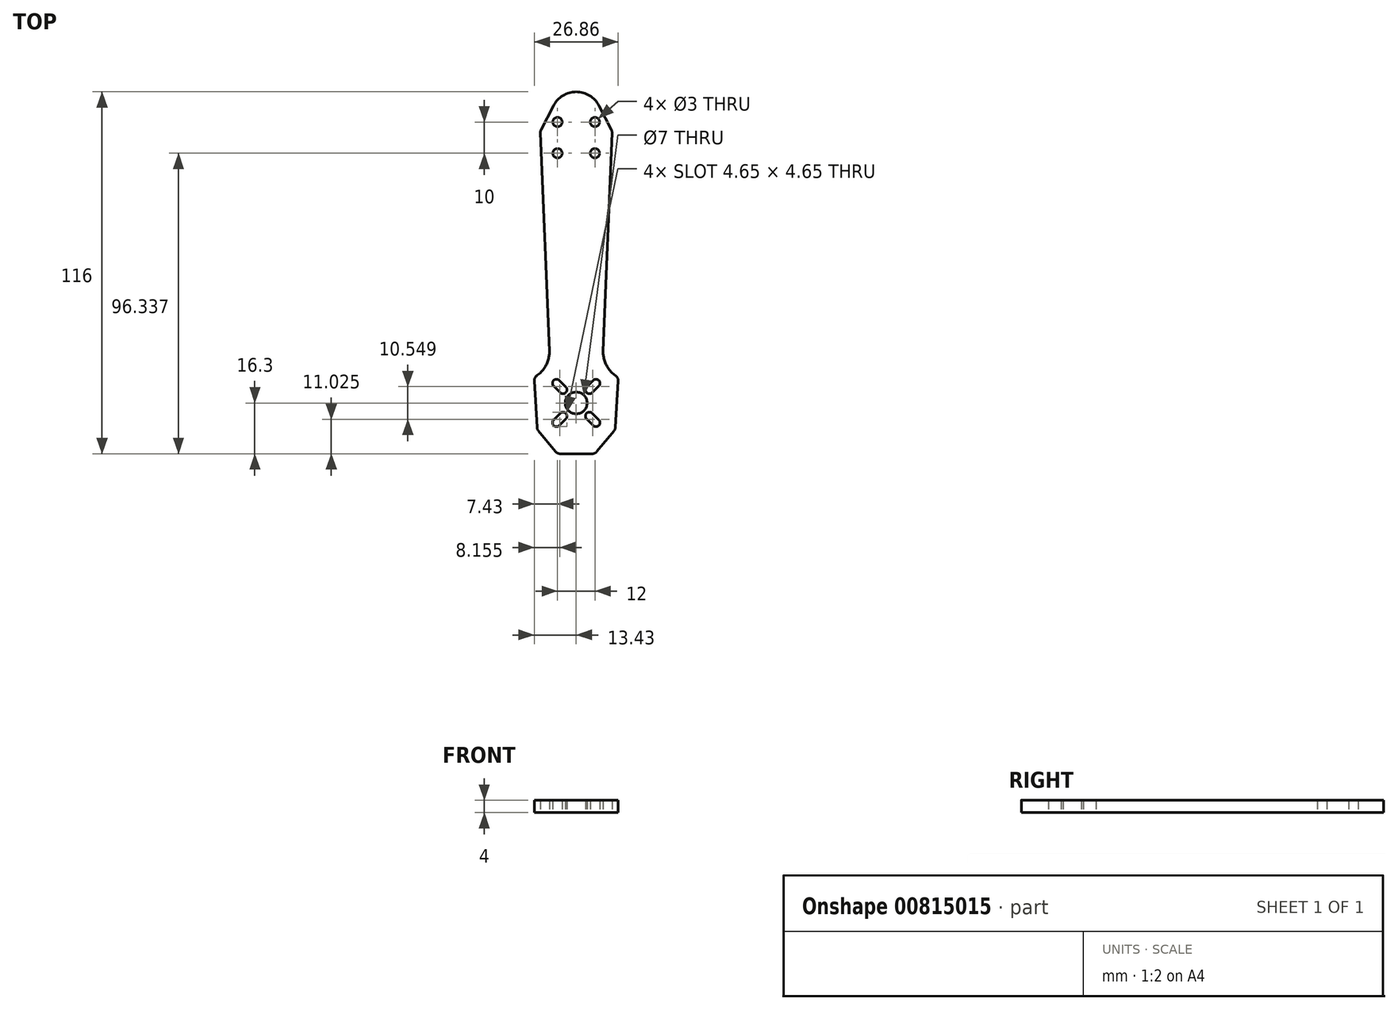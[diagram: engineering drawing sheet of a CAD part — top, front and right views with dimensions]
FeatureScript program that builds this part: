
annotation { "Feature Type Name" : "Feature", "Feature Type Description" : "" }
export const myFeature = defineFeature(function(context is Context, id is Id, definition is map)
    precondition{}
    {
        {
            var Q0;
            Q0=qCreatedBy(makeId("Top.planeOp"),FACE);
            var sketch = newSketch(context, id + "F0", { "sketchPlane" : qUnion([Q0])});
            skLineSegment(sketch, "E0", {"start": v(0, -16.3) * mm, "end": v(0, 99.7) * mm, "construction": true});
            skCircle(sketch, "E1", {"center": v(0, 0) * mm, "radius": 3.5 * mm});
            skLineSegment(sketch, "E2", {"start": v(-4.49, -4.49) * mm, "end": v(4.49, 4.49) * mm, "construction": true});
            skLineSegment(sketch, "E3", {"start": v(-4.02, 4.02) * mm, "end": v(4.02, -4.02) * mm, "construction": true});
            skLineSegment(sketch, "E4", {"start": v(4.25, -4.25) * mm, "end": v(6.3, -6.3) * mm, "construction": true});
            skArc(sketch, "E5.0.startCap", {"start": v(3.33, -5.17) * mm, "mid": v(3.33, -3.33) * mm, "end": v(5.17, -3.33) * mm});
            skArc(sketch, "E5.0.endCap", {"start": v(7.22, -5.38) * mm, "mid": v(7.22, -7.22) * mm, "end": v(5.38, -7.22) * mm});
            skLineSegment(sketch, "E5.0.left", {"start": v(5.17, -3.33) * mm, "end": v(7.22, -5.38) * mm});
            skLineSegment(sketch, "E5.0.right", {"start": v(3.33, -5.17) * mm, "end": v(5.38, -7.22) * mm});
            skLineSegment(sketch, "E6", {"start": v(-4.25, -4.25) * mm, "end": v(-6.3, -6.3) * mm, "construction": true});
            skArc(sketch, "E7.0.startCap", {"start": v(-5.17, -3.33) * mm, "mid": v(-3.33, -3.33) * mm, "end": v(-3.33, -5.17) * mm});
            skArc(sketch, "E7.0.endCap", {"start": v(-5.38, -7.22) * mm, "mid": v(-7.22, -7.22) * mm, "end": v(-7.22, -5.38) * mm});
            skLineSegment(sketch, "E7.0.left", {"start": v(-3.33, -5.17) * mm, "end": v(-5.38, -7.22) * mm});
            skLineSegment(sketch, "E7.0.right", {"start": v(-5.17, -3.33) * mm, "end": v(-7.22, -5.38) * mm});
            skLineSegment(sketch, "E8.MirrorCS", {"start": v(-4.25, 4.25) * mm, "end": v(-6.3, 6.3) * mm, "construction": true});
            skArc(sketch, "E9.MirrorCS", {"start": v(-5.17, 3.33) * mm, "mid": v(-3.33, 3.33) * mm, "end": v(-3.33, 5.17) * mm});
            skArc(sketch, "E10.MirrorCS", {"start": v(-5.38, 7.22) * mm, "mid": v(-7.22, 7.22) * mm, "end": v(-7.22, 5.38) * mm});
            skLineSegment(sketch, "E11.MirrorCS", {"start": v(-3.33, 5.17) * mm, "end": v(-5.38, 7.22) * mm});
            skLineSegment(sketch, "E12.MirrorCS", {"start": v(-5.17, 3.33) * mm, "end": v(-7.22, 5.38) * mm});
            skLineSegment(sketch, "E13.MirrorCS", {"start": v(5.17, 3.33) * mm, "end": v(7.22, 5.38) * mm});
            skLineSegment(sketch, "E14.MirrorCS", {"start": v(4.25, 4.25) * mm, "end": v(6.3, 6.3) * mm, "construction": true});
            skArc(sketch, "E15.MirrorCS", {"start": v(7.22, 5.38) * mm, "mid": v(7.22, 7.22) * mm, "end": v(5.38, 7.22) * mm});
            skArc(sketch, "E16.MirrorCS", {"start": v(3.33, 5.17) * mm, "mid": v(3.33, 3.33) * mm, "end": v(5.17, 3.33) * mm});
            skLineSegment(sketch, "E17.MirrorCS", {"start": v(3.33, 5.17) * mm, "end": v(5.38, 7.22) * mm});
            skCircle(sketch, "E18.1", {"center": v(6, 80.04) * mm, "radius": 1.5 * mm});
            skCircle(sketch, "E18.2", {"center": v(-6, 80.04) * mm, "radius": 1.5 * mm});
            skCircle(sketch, "E18.3", {"center": v(6, 90.04) * mm, "radius": 1.5 * mm});
            skCircle(sketch, "E18.4", {"center": v(-6, 90.04) * mm, "radius": 1.5 * mm});
            skLineSegment(sketch, "E19.bottom", {"start": v(6, 80.04) * mm, "end": v(-6, 80.04) * mm, "construction": true});
            skLineSegment(sketch, "E19.top", {"start": v(6, 90.04) * mm, "end": v(-6, 90.04) * mm, "construction": true});
            skLineSegment(sketch, "E19.left", {"start": v(6, 80.04) * mm, "end": v(6, 90.04) * mm, "construction": true});
            skLineSegment(sketch, "E19.right", {"start": v(-6, 80.04) * mm, "end": v(-6, 90.04) * mm, "construction": true});
            skPoint(sketch, "E19.middle", {"position": v(0, 85.04) * mm});
            skLineSegment(sketch, "E20", {"start": v(-6, -16.3) * mm, "end": v(-12.5, -8.5) * mm});
            skLineSegment(sketch, "E21", {"start": v(-12.5, -8.5) * mm, "end": v(-13.5, 8.2) * mm});
            skLineSegment(sketch, "E22", {"start": v(-8.6, 16.7) * mm, "end": v(-11.5, 87.04) * mm});
            skLineSegment(sketch, "E23", {"start": v(-11.5, 87.04) * mm, "end": v(-7.3, 95.24) * mm});
            skFitSpline(sketch, "E24", {"points": [v(-8.6, 16.7) * mm, v(-13.5, 8.2) * mm], "startDerivative": vector(0.32, -7.88) * mm, "endDerivative": vector(-11.17, -5.98) * mm});
            skLineSegment(sketch, "E25.MirrorCS", {"start": v(6, -16.3) * mm, "end": v(12.5, -8.5) * mm});
            skLineSegment(sketch, "E26.MirrorCS", {"start": v(12.5, -8.5) * mm, "end": v(13.5, 8.2) * mm});
            skFitSpline(sketch, "E27.MirrorCS", {"points": [v(8.6, 16.7) * mm, v(13.5, 8.2) * mm], "startDerivative": vector(-0.32, -7.88) * mm, "endDerivative": vector(11.17, -5.98) * mm});
            skLineSegment(sketch, "E28.MirrorCS", {"start": v(8.6, 16.7) * mm, "end": v(11.5, 87.04) * mm});
            skLineSegment(sketch, "E29.MirrorCS", {"start": v(11.5, 87.04) * mm, "end": v(7.3, 95.24) * mm});
            skArc(sketch, "E30", {"start": v(7.3, 95.24) * mm, "mid": v(0, 99.7) * mm, "end": v(-7.3, 95.24) * mm});
            skLineSegment(sketch, "E31", {"start": v(0, -16.3) * mm, "end": v(6, -16.3) * mm});
            skLineSegment(sketch, "E32.MirrorCS", {"start": v(0, -16.3) * mm, "end": v(-6, -16.3) * mm});
            skSolve(sketch);
        }
        {
            var Q0;
            Q0 = qSketchRegion(id + "F0", true);
            extrude(context, id + "F1", {"entities" : qUnion([Q0]), "depth" : 4 * mm, "offsetDistance" : 25 * mm});
        }
        {
            var Q0;
            Q0=makeQuery(id+"F1.opExtrude","SWEPT_EDGE",EDGE,{"disambiguationData":[OSD([sQuery(id+"F0.wireOp",EDGE,"E22"),sQuery(id+"F0.wireOp",EDGE,"E23")])]});
            var Q1;
            Q1=makeQuery(id+"F1.opExtrude","SWEPT_EDGE",EDGE,{"disambiguationData":[OSD([sQuery(id+"F0.wireOp",EDGE,"E28.MirrorCS"),sQuery(id+"F0.wireOp",EDGE,"E29.MirrorCS")])]});
            var Q2;
            Q2=makeQuery(id+"F1.opExtrude","SWEPT_EDGE",EDGE,{"disambiguationData":[OSD([sQuery(id+"F0.wireOp",EDGE,"E26.MirrorCS"),sQuery(id+"F0.wireOp",EDGE,"E27.MirrorCS")])]});
            var Q3;
            Q3=makeQuery(id+"F1.opExtrude","SWEPT_EDGE",EDGE,{"disambiguationData":[OSD([sQuery(id+"F0.wireOp",EDGE,"E21"),sQuery(id+"F0.wireOp",EDGE,"E24")])]});
            var Q4;
            Q4=makeQuery(id+"F1.opExtrude","SWEPT_EDGE",EDGE,{"disambiguationData":[OSD([sQuery(id+"F0.wireOp",EDGE,"E20"),sQuery(id+"F0.wireOp",EDGE,"E21")])]});
            var Q5;
            Q5=makeQuery(id+"F1.opExtrude","SWEPT_EDGE",EDGE,{"disambiguationData":[OSD([sQuery(id+"F0.wireOp",EDGE,"E25.MirrorCS"),sQuery(id+"F0.wireOp",EDGE,"E26.MirrorCS")])]});
            var Q6;
            Q6=makeQuery(id+"F1.opExtrude","SWEPT_EDGE",EDGE,{"disambiguationData":[OSD([sQuery(id+"F0.wireOp",EDGE,"E25.MirrorCS"),sQuery(id+"F0.wireOp",EDGE,"E31")])]});
            var Q7;
            Q7=makeQuery(id+"F1.opExtrude","SWEPT_EDGE",EDGE,{"disambiguationData":[OSD([sQuery(id+"F0.wireOp",EDGE,"9BPenLiq-MdgH-tJqK-gNSl-3rVMVTVlRtI7"),sQuery(id+"F0.wireOp",EDGE,"E20")])]});
            fillet(context, id + "F2", {"entities" : qUnion([Q0, Q1, Q2, Q3, Q4, Q5, Q6, Q7]), "radius" : 2 * mm, "tangentPropagation" : true, "allowEdgeOverflow" : false});
        }
    });
